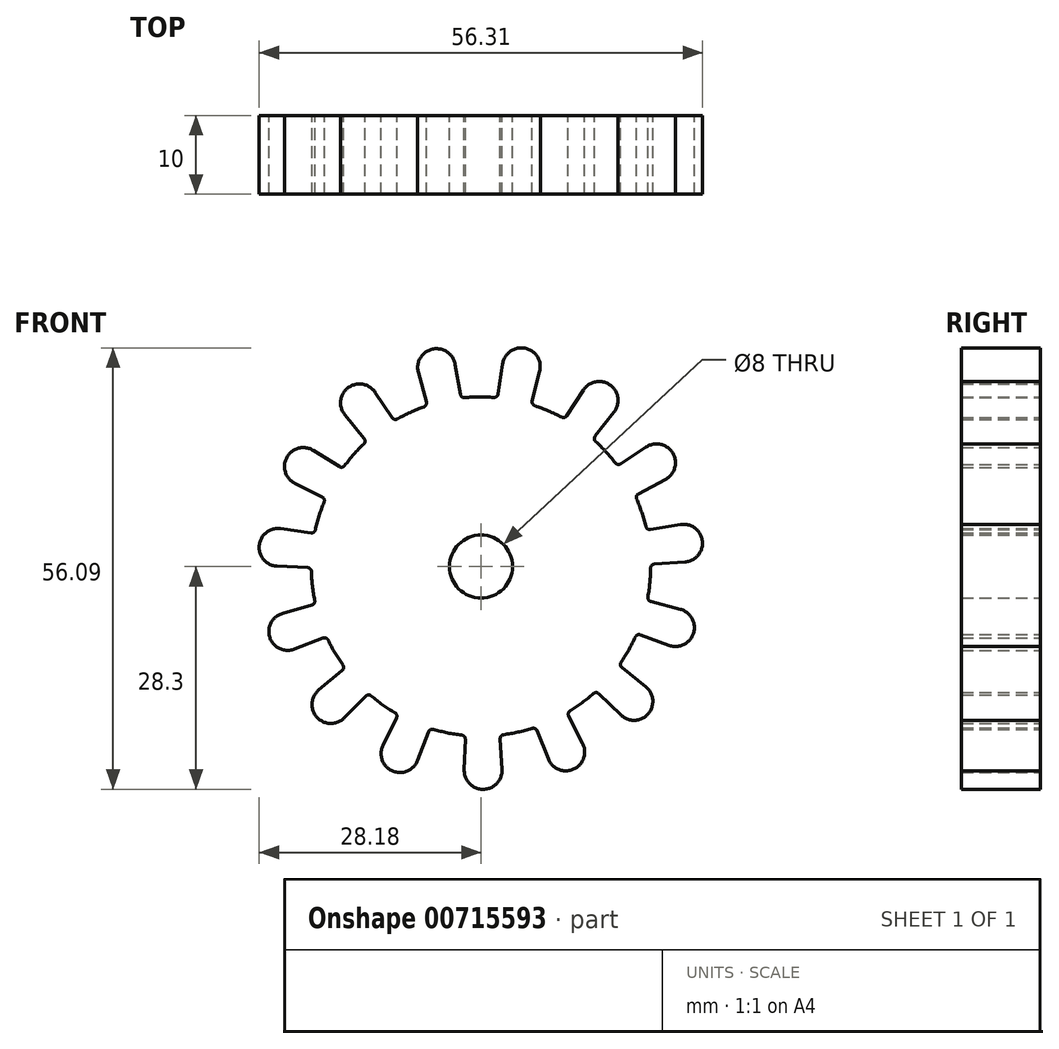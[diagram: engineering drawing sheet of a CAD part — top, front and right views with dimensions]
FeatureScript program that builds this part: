
annotation { "Feature Type Name" : "Feature", "Feature Type Description" : "" }
export const myFeature = defineFeature(function(context is Context, id is Id, definition is map)
    precondition{}
    {
        {
            var Q0;
            Q0=qCreatedBy(makeId("Front.planeOp"),FACE);
            var sketch = newSketch(context, id + "F0", { "sketchPlane" : qUnion([Q0])});
            skCircle(sketch, "E0", {"center": v(0, 0) * mm, "radius": 4 * mm});
            skCircle(sketch, "E1", {"center": v(0, 0) * mm, "radius": 25.9 * mm, "construction": true});
            skCircle(sketch, "E2", {"center": v(0, 0) * mm, "radius": 21.55 * mm});
            skCircle(sketch, "E3", {"center": v(15, 21.1) * mm, "radius": 2.4 * mm});
            skLineSegment(sketch, "E4", {"start": v(13, 22.4) * mm, "end": v(10.89, 19.14) * mm});
            skLineSegment(sketch, "E5", {"start": v(16.9, 19.63) * mm, "end": v(14.5, 16.57) * mm});
            skArc(sketch, "E6", {"start": v(14.5, 16.57) * mm, "mid": v(14.4, 16.22) * mm, "end": v(14.56, 15.9) * mm});
            skArc(sketch, "E7", {"start": v(10.23, 18.97) * mm, "mid": v(10.6, 18.92) * mm, "end": v(10.89, 19.14) * mm});
            skCircle(sketch, "E8.1.0", {"center": v(5.13, 25.39) * mm, "radius": 2.4 * mm});
            skLineSegment(sketch, "E8.1.1", {"start": v(2.75, 25.75) * mm, "end": v(2.16, 21.91) * mm});
            skArc(sketch, "E8.1.2", {"start": v(1.63, 21.49) * mm, "mid": v(1.98, 21.6) * mm, "end": v(2.16, 21.91) * mm});
            skArc(sketch, "E8.1.3", {"start": v(6.5, 21.03) * mm, "mid": v(6.56, 20.67) * mm, "end": v(6.83, 20.44) * mm});
            skLineSegment(sketch, "E8.1.4", {"start": v(7.45, 24.8) * mm, "end": v(6.5, 21.03) * mm});
            skCircle(sketch, "E9.1.2.0", {"center": v(-5.64, 25.28) * mm, "radius": 2.4 * mm});
            skLineSegment(sketch, "E9.2.2.0", {"start": v(-7.96, 24.65) * mm, "end": v(-6.94, 20.9) * mm});
            skArc(sketch, "E9.5.2.0", {"start": v(-7.25, 20.3) * mm, "mid": v(-6.98, 20.53) * mm, "end": v(-6.94, 20.9) * mm});
            skArc(sketch, "E9.9.2.0", {"start": v(-2.6, 21.86) * mm, "mid": v(-2.42, 21.55) * mm, "end": v(-2.07, 21.45) * mm});
            skLineSegment(sketch, "E9.13.2.0", {"start": v(-3.28, 25.7) * mm, "end": v(-2.6, 21.86) * mm});
            skCircle(sketch, "E9.1.3.0", {"center": v(-15.44, 20.8) * mm, "radius": 2.4 * mm});
            skLineSegment(sketch, "E9.2.3.0", {"start": v(-17.3, 19.28) * mm, "end": v(-14.84, 16.27) * mm});
            skArc(sketch, "E9.5.3.0", {"start": v(-14.88, 15.59) * mm, "mid": v(-14.72, 15.92) * mm, "end": v(-14.84, 16.27) * mm});
            skArc(sketch, "E9.9.3.0", {"start": v(-11.28, 18.91) * mm, "mid": v(-10.98, 18.7) * mm, "end": v(-10.61, 18.75) * mm});
            skLineSegment(sketch, "E9.13.3.0", {"start": v(-13.45, 22.14) * mm, "end": v(-11.28, 18.91) * mm});
            skCircle(sketch, "E9.1.4.0", {"center": v(-22.56, 12.72) * mm, "radius": 2.4 * mm});
            skLineSegment(sketch, "E9.2.4.0", {"start": v(-23.64, 10.58) * mm, "end": v(-20.17, 8.83) * mm});
            skArc(sketch, "E9.5.4.0", {"start": v(-19.93, 8.2) * mm, "mid": v(-19.93, 8.55) * mm, "end": v(-20.17, 8.83) * mm});
            skArc(sketch, "E9.9.4.0", {"start": v(-18, 12.69) * mm, "mid": v(-17.63, 12.62) * mm, "end": v(-17.32, 12.82) * mm});
            skLineSegment(sketch, "E9.13.4.0", {"start": v(-21.29, 14.75) * mm, "end": v(-18, 12.69) * mm});
            skCircle(sketch, "E9.1.5.0", {"center": v(-25.78, 2.44) * mm, "radius": 2.4 * mm});
            skLineSegment(sketch, "E9.2.5.0", {"start": v(-25.9, 0.05) * mm, "end": v(-22.02, -0.14) * mm});
            skArc(sketch, "E9.5.5.0", {"start": v(-21.54, -0.63) * mm, "mid": v(-21.68, -0.29) * mm, "end": v(-22.02, -0.14) * mm});
            skArc(sketch, "E9.9.5.0", {"start": v(-21.6, 4.27) * mm, "mid": v(-21.24, 4.36) * mm, "end": v(-21.04, 4.66) * mm});
            skLineSegment(sketch, "E9.13.5.0", {"start": v(-25.45, 4.82) * mm, "end": v(-21.6, 4.27) * mm});
            skCircle(sketch, "E9.1.6.0", {"center": v(-24.55, -8.25) * mm, "radius": 2.4 * mm});
            skLineSegment(sketch, "E9.2.6.0", {"start": v(-23.68, -10.5) * mm, "end": v(-20.06, -9.08) * mm});
            skArc(sketch, "E9.5.6.0", {"start": v(-19.42, -9.33) * mm, "mid": v(-19.7, -9.08) * mm, "end": v(-20.06, -9.08) * mm});
            skArc(sketch, "E9.9.6.0", {"start": v(-21.47, -4.88) * mm, "mid": v(-21.18, -4.66) * mm, "end": v(-21.12, -4.3) * mm});
            skLineSegment(sketch, "E9.13.6.0", {"start": v(-25.2, -5.95) * mm, "end": v(-21.47, -4.88) * mm});
            skCircle(sketch, "E9.1.7.0", {"center": v(-19.07, -17.53) * mm, "radius": 2.4 * mm});
            skLineSegment(sketch, "E9.2.7.0", {"start": v(-17.37, -19.22) * mm, "end": v(-14.63, -16.46) * mm});
            skArc(sketch, "E9.5.7.0", {"start": v(-13.95, -16.43) * mm, "mid": v(-14.3, -16.3) * mm, "end": v(-14.63, -16.46) * mm});
            skArc(sketch, "E9.9.7.0", {"start": v(-17.63, -13.2) * mm, "mid": v(-17.45, -12.87) * mm, "end": v(-17.54, -12.52) * mm});
            skLineSegment(sketch, "E9.13.7.0", {"start": v(-20.6, -15.69) * mm, "end": v(-17.63, -13.2) * mm});
            skCircle(sketch, "E9.1.8.0", {"center": v(-10.3, -23.77) * mm, "radius": 2.4 * mm});
            skLineSegment(sketch, "E9.2.8.0", {"start": v(-8.05, -24.62) * mm, "end": v(-6.67, -20.98) * mm});
            skArc(sketch, "E9.5.8.0", {"start": v(-6.06, -20.68) * mm, "mid": v(-6.43, -20.71) * mm, "end": v(-6.67, -20.98) * mm});
            skArc(sketch, "E9.9.8.0", {"start": v(-10.74, -19.22) * mm, "mid": v(-10.7, -18.86) * mm, "end": v(-10.93, -18.57) * mm});
            skLineSegment(sketch, "E9.13.8.0", {"start": v(-12.45, -22.71) * mm, "end": v(-10.74, -19.22) * mm});
            skCircle(sketch, "E9.1.9.0", {"center": v(0.26, -25.9) * mm, "radius": 2.4 * mm});
            skLineSegment(sketch, "E9.2.9.0", {"start": v(2.66, -25.76) * mm, "end": v(2.44, -21.88) * mm});
            skArc(sketch, "E9.5.9.0", {"start": v(2.87, -21.36) * mm, "mid": v(2.55, -21.53) * mm, "end": v(2.44, -21.88) * mm});
            skArc(sketch, "E9.9.9.0", {"start": v(-2, -21.93) * mm, "mid": v(-2.11, -21.58) * mm, "end": v(-2.44, -21.41) * mm});
            skLineSegment(sketch, "E9.13.9.0", {"start": v(-2.13, -25.81) * mm, "end": v(-2, -21.93) * mm});
            skCircle(sketch, "E9.1.10.0", {"center": v(10.78, -23.55) * mm, "radius": 2.4 * mm});
            skLineSegment(sketch, "E9.2.10.0", {"start": v(12.9, -22.45) * mm, "end": v(11.13, -19) * mm});
            skArc(sketch, "E9.5.10.0", {"start": v(11.31, -18.34) * mm, "mid": v(11.1, -18.63) * mm, "end": v(11.13, -19) * mm});
            skArc(sketch, "E9.9.10.0", {"start": v(7.1, -20.84) * mm, "mid": v(6.85, -20.58) * mm, "end": v(6.48, -20.55) * mm});
            skLineSegment(sketch, "E9.13.10.0", {"start": v(8.55, -24.45) * mm, "end": v(7.1, -20.84) * mm});
            skCircle(sketch, "E9.1.11.0", {"center": v(19.42, -17.13) * mm, "radius": 2.4 * mm});
            skLineSegment(sketch, "E9.2.11.0", {"start": v(20.93, -15.26) * mm, "end": v(17.9, -12.83) * mm});
            skArc(sketch, "E9.5.11.0", {"start": v(17.8, -12.16) * mm, "mid": v(17.71, -12.51) * mm, "end": v(17.9, -12.83) * mm});
            skArc(sketch, "E9.9.11.0", {"start": v(14.96, -16.15) * mm, "mid": v(14.62, -16.01) * mm, "end": v(14.28, -16.14) * mm});
            skLineSegment(sketch, "E9.13.11.0", {"start": v(17.75, -18.86) * mm, "end": v(14.96, -16.15) * mm});
            skCircle(sketch, "E9.1.12.0", {"center": v(24.71, -7.75) * mm, "radius": 2.4 * mm});
            skLineSegment(sketch, "E9.2.12.0", {"start": v(25.32, -5.43) * mm, "end": v(21.56, -4.44) * mm});
            skArc(sketch, "E9.5.12.0", {"start": v(21.2, -3.87) * mm, "mid": v(21.27, -4.22) * mm, "end": v(21.56, -4.44) * mm});
            skArc(sketch, "E9.9.12.0", {"start": v(20.24, -8.67) * mm, "mid": v(19.87, -8.68) * mm, "end": v(19.61, -8.93) * mm});
            skLineSegment(sketch, "E9.13.12.0", {"start": v(23.89, -10) * mm, "end": v(20.24, -8.67) * mm});
            skCircle(sketch, "E9.1.13.0", {"center": v(25.73, 2.97) * mm, "radius": 2.4 * mm});
            skLineSegment(sketch, "E9.2.13.0", {"start": v(25.34, 5.34) * mm, "end": v(21.5, 4.71) * mm});
            skArc(sketch, "E9.5.13.0", {"start": v(20.94, 5.1) * mm, "mid": v(21.15, 4.8) * mm, "end": v(21.5, 4.71) * mm});
            skArc(sketch, "E9.9.13.0", {"start": v(22.01, 0.3) * mm, "mid": v(21.69, 0.15) * mm, "end": v(21.55, -0.18) * mm});
            skLineSegment(sketch, "E9.13.13.0", {"start": v(25.9, 0.58) * mm, "end": v(22.01, 0.3) * mm});
            skCircle(sketch, "E9.1.14.0", {"center": v(22.3, 13.18) * mm, "radius": 2.4 * mm});
            skLineSegment(sketch, "E9.2.14.0", {"start": v(20.98, 15.19) * mm, "end": v(17.73, 13.05) * mm});
            skArc(sketch, "E9.5.14.0", {"start": v(17.06, 13.17) * mm, "mid": v(17.37, 12.98) * mm, "end": v(17.73, 13.05) * mm});
            skArc(sketch, "E9.9.14.0", {"start": v(19.99, 9.24) * mm, "mid": v(19.75, 8.96) * mm, "end": v(19.76, 8.6) * mm});
            skLineSegment(sketch, "E9.13.14.0", {"start": v(23.42, 11.06) * mm, "end": v(19.99, 9.24) * mm});
            skSolve(sketch);
        }
        {
            var Q0;
            Q0 = qSketchRegion(id + "F0", true);
            extrude(context, id + "F1", {"entities" : qUnion([Q0]), "depth" : 10 * mm, "offsetDistance" : 25 * mm});
        }
    });
